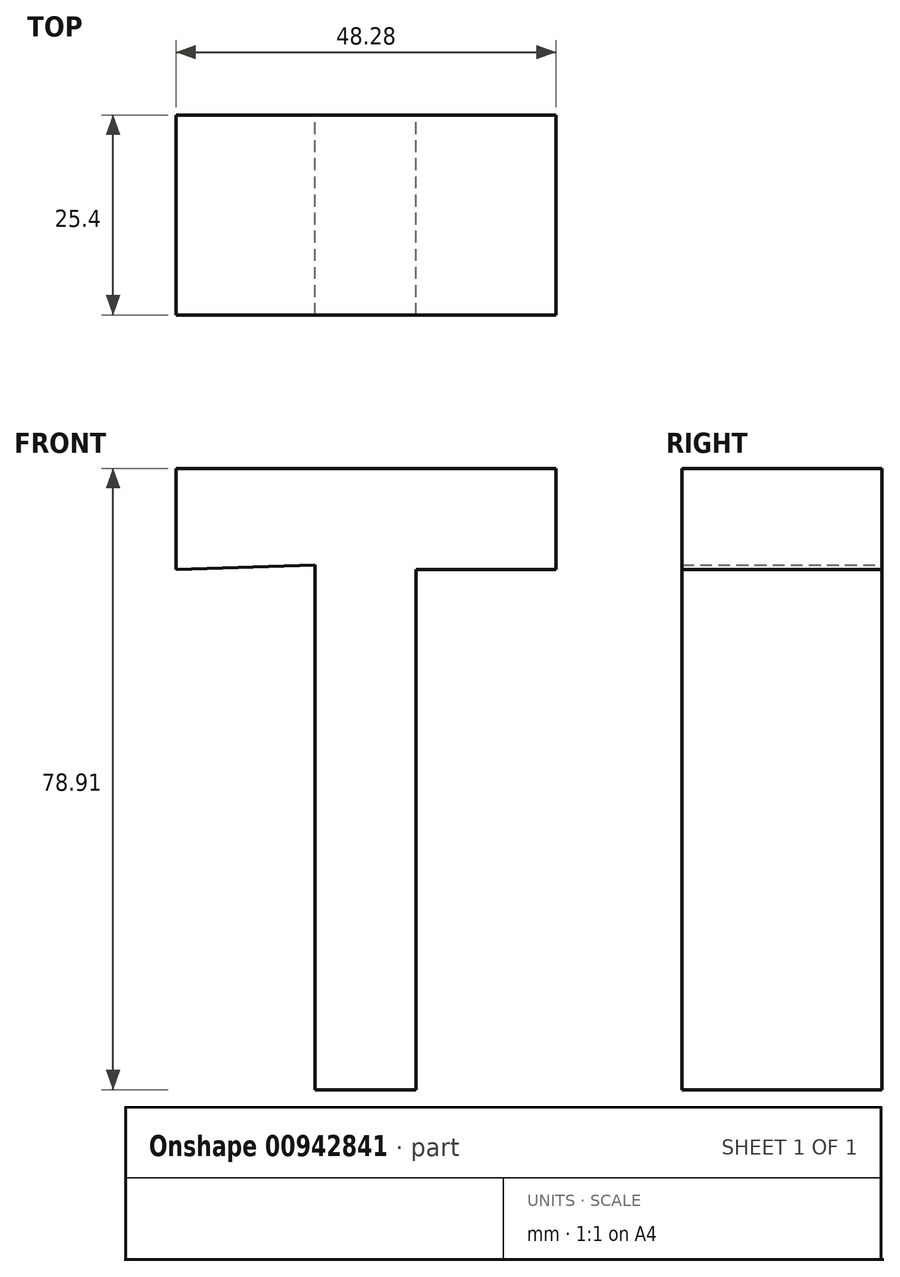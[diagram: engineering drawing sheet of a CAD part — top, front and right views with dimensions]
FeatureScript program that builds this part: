
annotation { "Feature Type Name" : "Feature", "Feature Type Description" : "" }
export const myFeature = defineFeature(function(context is Context, id is Id, definition is map)
    precondition{}
    {
        {
            var Q0;
            Q0=qCreatedBy(makeId("Front.planeOp"),FACE);
            var sketch = newSketch(context, id + "F0", { "sketchPlane" : qUnion([Q0])});
            skLineSegment(sketch, "E0", {"start": v(-42.97, 35.66) * mm, "end": v(-42.97, -30.97) * mm});
            skLineSegment(sketch, "E1", {"start": v(-42.97, -30.97) * mm, "end": v(-30.14, -30.97) * mm});
            skLineSegment(sketch, "E2", {"start": v(-30.14, -30.97) * mm, "end": v(-30.14, 35.1) * mm});
            skLineSegment(sketch, "E3", {"start": v(-30.14, 35.1) * mm, "end": v(-12.35, 35.1) * mm});
            skLineSegment(sketch, "E4", {"start": v(-12.35, 35.1) * mm, "end": v(-12.35, 39.1) * mm});
            skLineSegment(sketch, "E5", {"start": v(-12.35, 47.94) * mm, "end": v(-60.63, 47.94) * mm});
            skLineSegment(sketch, "E6", {"start": v(-60.63, 47.94) * mm, "end": v(-60.63, 35.1) * mm});
            skLineSegment(sketch, "E7", {"start": v(-60.63, 35.1) * mm, "end": v(-42.97, 35.66) * mm});
            skLineSegment(sketch, "E8", {"start": v(-12.35, 39.1) * mm, "end": v(-12.35, 47.94) * mm});
            skSolve(sketch);
        }
        {
            var Q0;
            Q0 = qSketchRegion(id + "F0", true);
            extrude(context, id + "F1", {"entities" : qUnion([Q0]), "depth" : 25.4 * mm, "offsetDistance" : 25.4 * mm});
        }
    });
